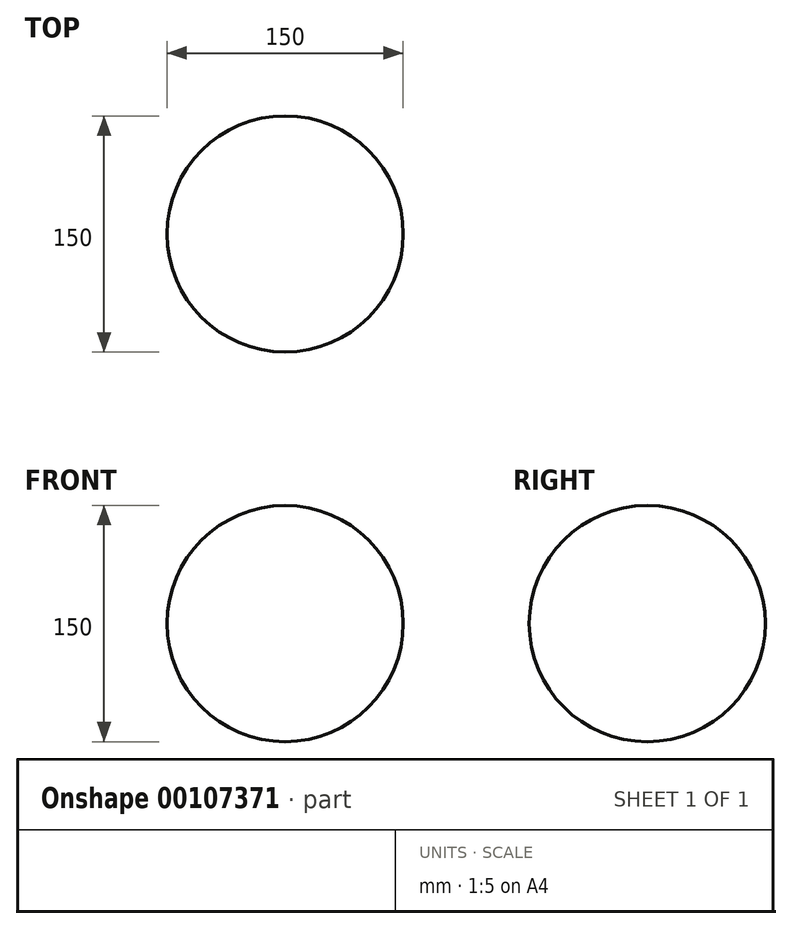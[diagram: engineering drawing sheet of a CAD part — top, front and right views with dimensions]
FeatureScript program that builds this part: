
annotation { "Feature Type Name" : "Feature", "Feature Type Description" : "" }
export const myFeature = defineFeature(function(context is Context, id is Id, definition is map)
    precondition{}
    {
        {
            var Q0;
            Q0=qCreatedBy(makeId("Front.planeOp"),FACE);
            var sketch = newSketch(context, id + "F0", { "sketchPlane" : qUnion([Q0])});
            skPoint(sketch, "E0", {"position": v(75, 0) * mm});
            skArc(sketch, "E1", {"start": v(0, -75) * mm, "mid": v(75, 0) * mm, "end": v(0, 75) * mm});
            skLineSegment(sketch, "E2", {"start": v(0, 0) * mm, "end": v(0, -163.7) * mm});
            skLineSegment(sketch, "E3", {"start": v(0, 153.18) * mm, "end": v(0, 0) * mm});
            skSolve(sketch);
        }
        {
            var Q0;
            {var subQ0=sQuery(id+"F0.wireOp",EDGE,"E1");Q0=makeQuery(id+"F0.imprint","IMPRINT",FACE,{"disambiguationData":[TD([[makeQuery(id+"F0.imprint","IMPRINT",EDGE,{"derivedFrom":subQ0}),1.0]])]});}
            var Q1;
            Q1=sQuery(id+"F0.wireOp",EDGE,"E3");
            revolve(context, id + "F1", {"entities" : qUnion([Q0]), "axis" : qUnion([Q1]), "revolveType" : RevolveType.FULL});
        }
    });
